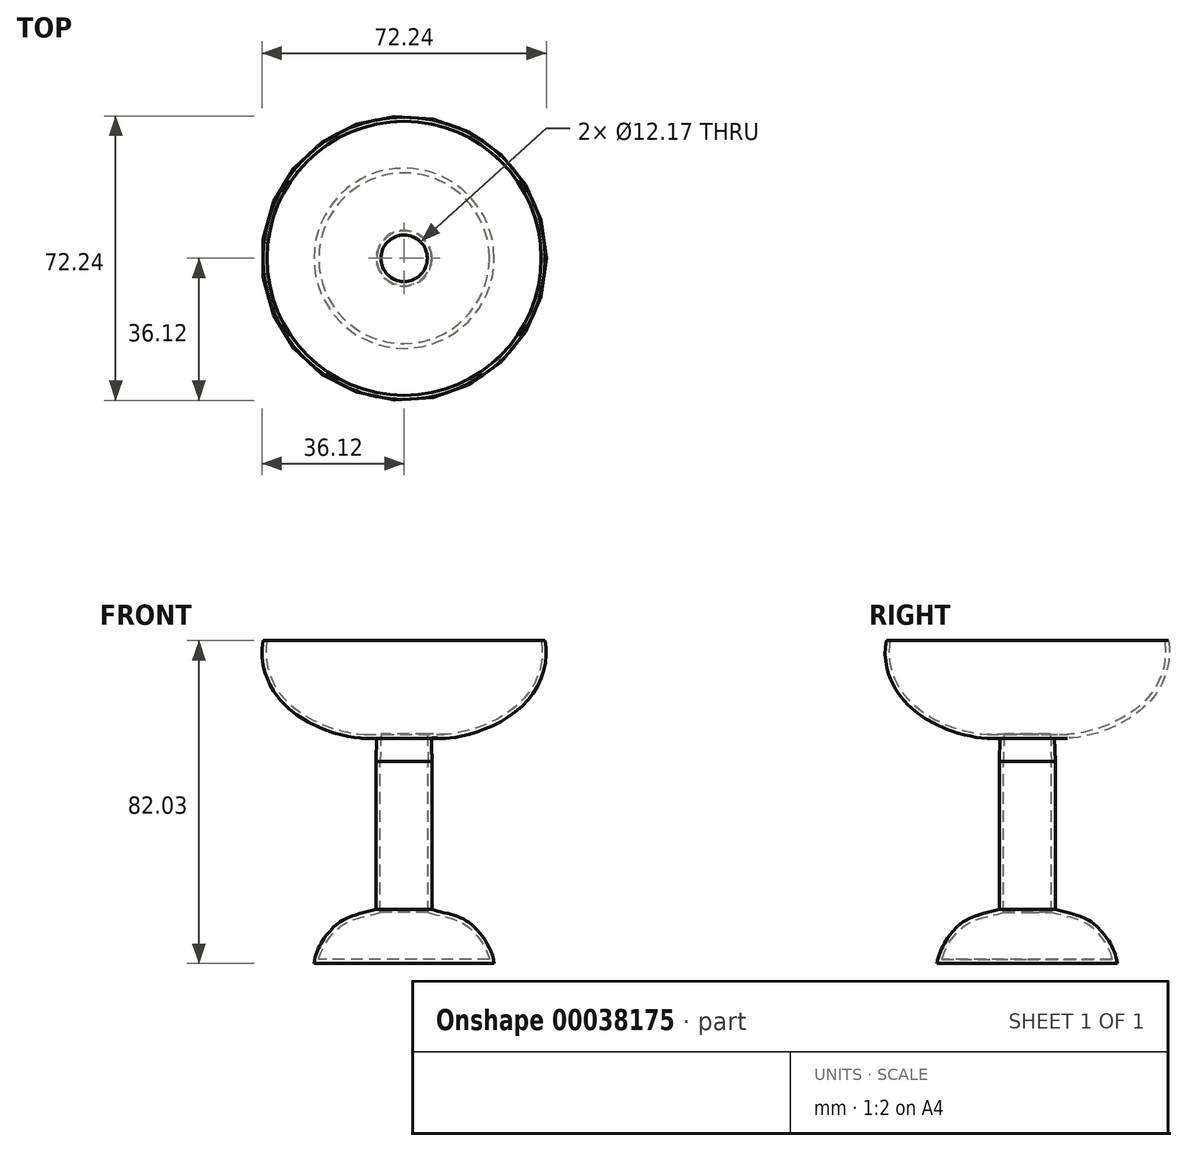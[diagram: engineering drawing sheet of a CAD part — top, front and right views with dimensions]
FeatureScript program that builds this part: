
annotation { "Feature Type Name" : "Feature", "Feature Type Description" : "" }
export const myFeature = defineFeature(function(context is Context, id is Id, definition is map)
    precondition{}
    {
        {
            var Q0;
            Q0=qCreatedBy(makeId("Front.planeOp"),FACE);
            var sketch = newSketch(context, id + "F0", { "sketchPlane" : qUnion([Q0])});
            skLineSegment(sketch, "E0", {"start": v(0, 42.8) * mm, "end": v(0, -39.22) * mm});
            skLineSegment(sketch, "E1", {"start": v(0, -39.22) * mm, "end": v(22.89, -39.22) * mm});
            skLineSegment(sketch, "E2", {"start": v(0, 42.8) * mm, "end": v(35.84, 42.8) * mm});
            skLineSegment(sketch, "E3", {"start": v(7.09, 12.12) * mm, "end": v(7.09, -25.53) * mm});
            skFitSpline(sketch, "E4", {"points": [v(35.84, 42.8) * mm, v(33.56, 30.6) * mm, v(21.94, 20.9) * mm, v(11.36, 18.03) * mm, v(6.93, 18.05) * mm], "startDerivative": vector(8.32, -39.53) * mm, "endDerivative": vector(-41.22, 0.17) * mm});
            skLineSegment(sketch, "E5", {"start": v(6.93, 18.05) * mm, "end": v(7.09, 12.12) * mm});
            skFitSpline(sketch, "E6", {"points": [v(7.09, -25.53) * mm, v(16.41, -28.79) * mm, v(22.89, -39.22) * mm], "startDerivative": vector(26.5, -7.37) * mm, "endDerivative": vector(3.26, -23.68) * mm});
            skSolve(sketch);
        }
        {
            var Q0;
            Q0=makeQuery(id+"F0.imprint","IMPRINT",FACE,{"disambiguationData":[TD([[makeQuery(id+"F0.imprint","IMPRINT",EDGE,{"derivedFrom":sQuery(id+"F0.wireOp",EDGE,"E0")}),1.0]])]});
            var Q1;
            Q1=sQuery(id+"F0.wireOp",EDGE,"E0");
            revolve(context, id + "F1", {"entities" : qUnion([Q0]), "axis" : qUnion([Q1]), "revolveType" : RevolveType.FULL});
        }
        {
            var Q0;
            Q0=makeQuery(id+"F1.opRevolve","SWEPT_FACE",FACE,{"disambiguationData":[OSD([sQuery(id+"F0.wireOp",EDGE,"E2")])]});
            shell(context, id + "F2", {"entities" : qUnion([Q0]), "thickness" : 1 * mm});
        }
    });
